# Revit family: ledwaterproof-p5-l15-62_72w-840_531000039100_7638
name_source: partatom
category: Lighting Fixtures
units: mm (PartAtom-declared; Revit-internal decimal feet)

## family parameters
Cut with Voids When Loaded = No
Host = Face
Light Source = No
Part Type = Normal
Room Calculation Point = No
Round Connector Dimension = Use Diameter
Shared = No

## types (1)
- LEDWaterproof-P5-L15-62/72W-840 (1 x LED, 6566 lm, 4000)
    Apparent Load = 72 VA
    Approval mark = CE, ENEC
    CIE Flux Codes = 41 70 89 88 100
    Color Rendering = 80
    Color Temperature = 4000
    Control Gear = Electronic ballast
    Default Elevation = 1800 mm
    Description = Waterproof Performer G5 1580mm-62|72W-6566lm-4000K-IP66
    Frequency = 60 Hz
    Height = 71 mm
    Lamp = 1 x LED
    Lamp Light Flux = 6566 lm
    Lamp count = 1
    Length = 1580 mm
    Luminous efficacy = 91 lm/W
    Manufacturer = OPPLE
    ModVariant = No
    Model = 531000039100
    Number of Poles = 1
    OnlyDefault = Yes
    Power Factor = 1
    Product Name = LEDWaterproof-P5-L15-62/72W-840
    Product group = Ceiling / wall-mounted luminaires
    ProductGroupID = 30
    Protection Class = Protection class II
    Protection Degree = IP 66
    RLX_Detail_Level = 1
    RLX_Emergency_Light_Flux = 0 lm
    RLX_Emergency_Type = 0
    RLX_Emergency_Type_DB = No
    RlxData = <blob elided: 94369 chars, md5=5eedba29>
    Socket = socket
    Standby Power = 0 W
    System Light Flux = 6566 lm
    System Power = 72 W
    Type Comments = LED E C module 12W 2700K Clio CT
    Type Image = web_wp_p5.jpg
    URL = http://relux.com
    VarID = ---
    Voltage = 230 V
    Voltage Range = 220-240 V
    Weight = 0.00 kg
    Width = 73 mm

## geometry (parser evidence)
native form markers: Blend x4, Sweep x14
no freeform markers — native parametric forms only
